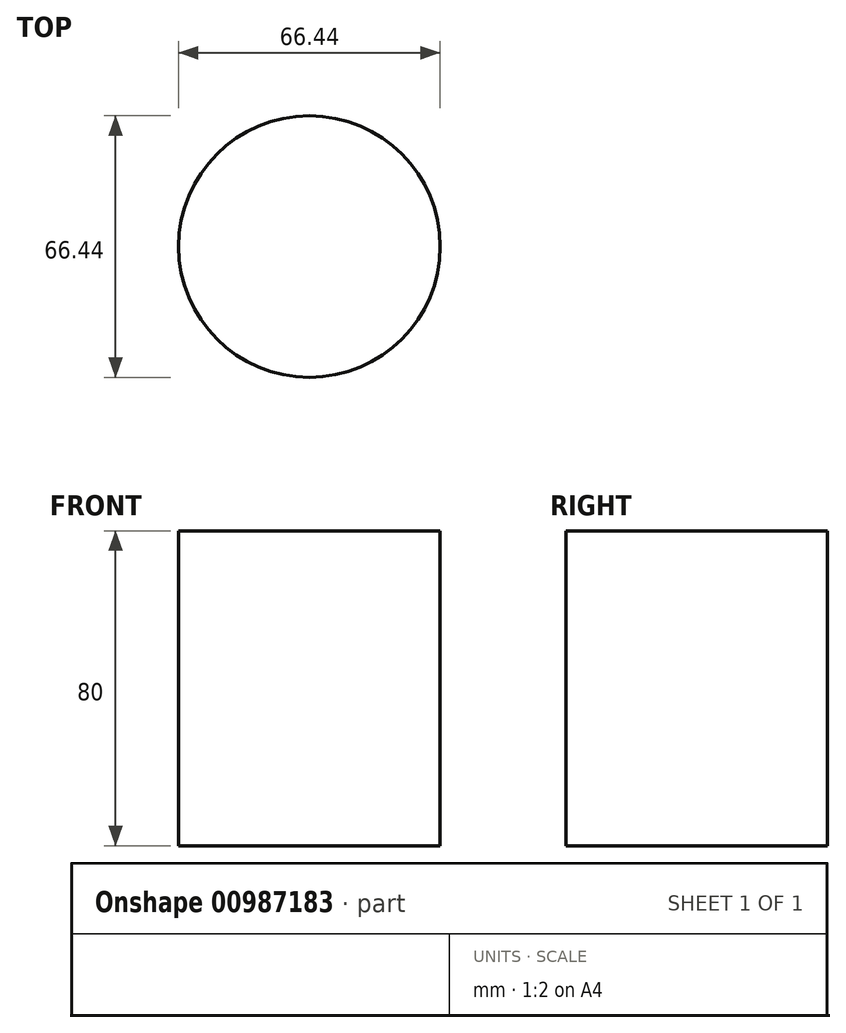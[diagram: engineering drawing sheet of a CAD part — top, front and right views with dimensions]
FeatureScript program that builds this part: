
annotation { "Feature Type Name" : "Feature", "Feature Type Description" : "" }
export const myFeature = defineFeature(function(context is Context, id is Id, definition is map)
    precondition{}
    {
        {
            var Q0;
            Q0=qCreatedBy(makeId("Top.planeOp"),FACE);
            var sketch = newSketch(context, id + "F0", { "sketchPlane" : qUnion([Q0])});
            skCircle(sketch, "E0", {"center": v(0, 0) * mm, "radius": 33.22 * mm});
            skSolve(sketch);
        }
        {
            var Q0;
            Q0=makeQuery(id+"F0.imprint","IMPRINT",FACE,{"disambiguationData":[TD([[makeQuery(id+"F0.imprint","IMPRINT",EDGE,{"derivedFrom":sQuery(id+"F0.wireOp",EDGE,"E0")}),1.0]])]});
            extrude(context, id + "F1", {"entities" : qUnion([Q0]), "oppositeDirection" : true, "depth" : 80 * mm, "offsetDistance" : 25.4 * mm});
        }
        {
            var Q0;
            Q0=makeQuery(id+"F1.opExtrude","CAP_FACE",FACE,{"disambiguationData":[OSD([sQuery(id+"F0.wireOp",EDGE,"E0")])],"isStart":true});
            var sketch = newSketch(context, id + "F2", { "sketchPlane" : qUnion([Q0])});
            skCircle(sketch, "E1", {"center": v(0, 0) * mm, "radius": 21.83 * mm});
            skSolve(sketch);
        }
        {
            var Q0;
            Q0 = qSketchRegion(id + "F2", true);
            extrude(context, id + "F3", {"entities" : qUnion([Q0]), "operationType" : NewBodyOperationType.ADD, "endBound" : BoundingType.UP_TO_NEXT, "oppositeDirection" : true, "depth" : 25.4 * mm, "offsetDistance" : 25.4 * mm});
        }
    });
